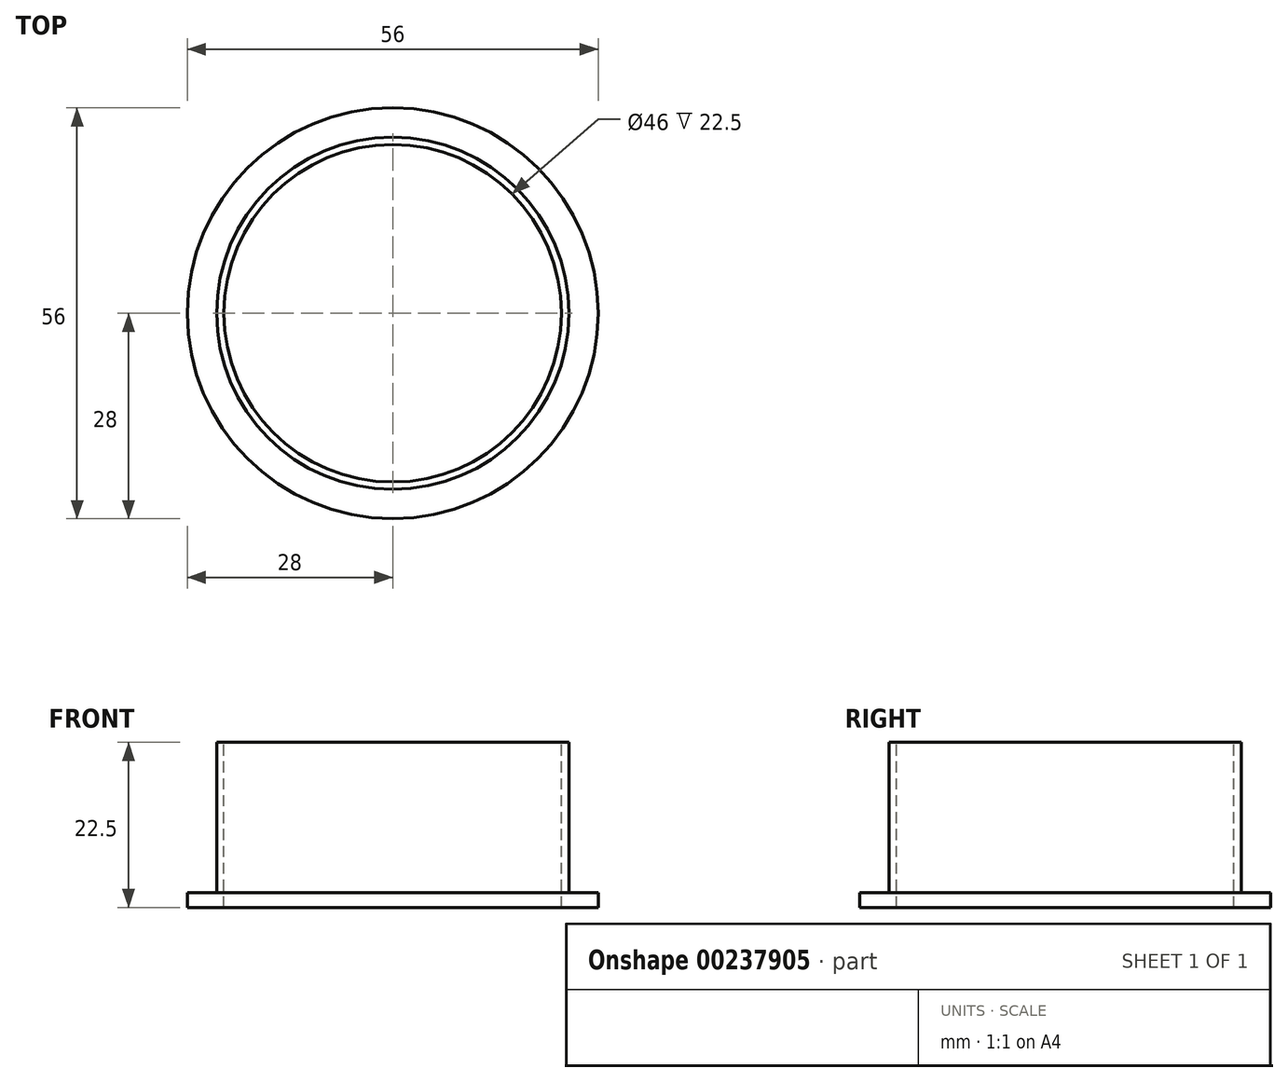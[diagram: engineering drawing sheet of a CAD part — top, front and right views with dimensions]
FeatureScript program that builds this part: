
annotation { "Feature Type Name" : "Feature", "Feature Type Description" : "" }
export const myFeature = defineFeature(function(context is Context, id is Id, definition is map)
    precondition{}
    {
        {
            var Q0;
            Q0=qCreatedBy(makeId("Top.planeOp"),FACE);
            var sketch = newSketch(context, id + "F0", { "sketchPlane" : qUnion([Q0])});
            skCircle(sketch, "E0", {"center": v(0, 0) * mm, "radius": 24 * mm});
            skCircle(sketch, "E1", {"center": v(0, 0) * mm, "radius": 23 * mm});
            skCircle(sketch, "E2", {"center": v(0, 0) * mm, "radius": 28 * mm});
            skSolve(sketch);
        }
        {
            var Q0;
            Q0=makeQuery(id+"F0.imprint","IMPRINT",FACE,{"disambiguationData":[TD([[makeQuery(id+"F0.imprint","IMPRINT",EDGE,{"derivedFrom":sQuery(id+"F0.wireOp",EDGE,"E0")}),-1.0]])]});
            var Q1;
            Q1=makeQuery(id+"F0.imprint","IMPRINT",FACE,{"disambiguationData":[TD([[makeQuery(id+"F0.imprint","IMPRINT",EDGE,{"derivedFrom":sQuery(id+"F0.wireOp",EDGE,"E0")}),1.0]])]});
            extrude(context, id + "F1", {"entities" : qUnion([Q0, Q1]), "oppositeDirection" : true, "depth" : 2 * mm, "offsetDistance" : 25 * mm});
        }
        {
            var Q0;
            Q0=makeQuery(id+"F0.imprint","IMPRINT",FACE,{"disambiguationData":[TD([[makeQuery(id+"F0.imprint","IMPRINT",EDGE,{"derivedFrom":sQuery(id+"F0.wireOp",EDGE,"E0")}),1.0]])]});
            extrude(context, id + "F2", {"entities" : qUnion([Q0]), "operationType" : NewBodyOperationType.ADD, "depth" : 20.5 * mm, "offsetDistance" : 25 * mm});
        }
    });
